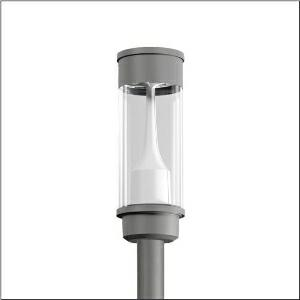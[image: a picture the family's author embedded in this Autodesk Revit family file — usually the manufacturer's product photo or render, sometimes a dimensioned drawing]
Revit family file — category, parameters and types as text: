
# Revit family: litepole_iq___pl1_2s_5xa5415of14h_b306
name_source: partatom
category: Lighting Fixtures
units: mm (PartAtom-declared; Revit-internal decimal feet)

## family parameters
Cut with Voids When Loaded = No
Host = Face
Light Source = No
Part Type = Normal
Room Calculation Point = No
Round Connector Dimension = Use Diameter
Shared = No

## types (1)
- --- (1 x LED, 2970 lm, 21.8 W, 2700K)
    Apparent Load = 22 VA
    CIE Flux Codes = 23 62 94 96 100
    Color Rendering = 70
    Color Temperature = 2700K
    Default Elevation = 1800 mm
    Description = Litepole iQ, mast luminaire, Module 540 iQ-SR, primary light control with 3 zone facetted reflector, of plastic, silver coated, highly specular, structured, primary optical cover: cover, of PMMA, transparent, partly coated, light distribution: PL1.2s, light emission: direct distribution, primary light characteristic: symmetric, installation type: post-top, LED, High Power LED, rated luminous flux: 2.970lm, luminous efficacy: 136lm/W, light colour: 727, colour temperature: 2700K, control gear: iQ Street-Remote, control: optimised constant luminous flux control (CLO 2.0), Desk-Remote (wireless, voltage-free reading and setting of iQ features in the workshop via application-optimized NFC function/RFID function), Light-Fading, Smart-Wire, Night-Set, Lumen-Switch, Temp-Guard, Auto-Match, Street-Remote, pre-setting: logarithmic dimming characteristic, with terminal, 6-pole, max. 2.5mm², mains connection: 230..240V, AC, 50/60Hz, start of lifetime: 22W, end of service life: 23W, reduction: 11W, luminaire housing, upper part, of glass-fibre reinforced polyester, coated, Siteco® metallic grey (DB 702S), diameter: 210mm, height: 590mm, spigot size: d x l = 76 x 70mm (post-top) | with reducer (optional accessory) 60 x 70mm, mounting height: 3..5m, post-top mast mounting element, of diecast aluminium, coated, Siteco® metallic grey (DB 702S), Module 540 iQ-SR, traffic white (RAL 9016), equipment: standard, protection rating (complete): IP65, insulation class (complete): insulation class II (safety insulation), certification: CE, ENEC, VDE, packaging unit: 1 piece

Light Distribution: PL1.2s
    Height = 590 mm
    Lamp = 1 x LED
    Lamp Light Flux = 2970 lm
    Lamp Power = 21.8 W
    Lamp count = 1
    Length = 220 mm
    Luminous efficacy = 136 lm/W
    Manufacturer = Siteco
    ModVariant = No
    Model = 5XA5415OF14H
    Number of Poles = 1
    OnlyDefault = Yes
    Power Factor = 1
    Product Name = Litepole iQ | PL1.2s
    Product group = mast luminaire | pylon top
    ProductGroupID = 6100
    Protection Class = Protection class II
    Protection Degree = IP 65
    RLX_Detail_Level = 1
    RLX_Emergency_Light_Flux = 0 lm
    RLX_Emergency_Type = 0
    RLX_Emergency_Type_DB = No
    RlxData = <blob elided: 40057 chars, md5=e18988a2>
    Socket = socket
    Standby Power = 0 W
    System Light Flux = 2970 lm
    System Power = 22 W
    Type Comments = factory setting: luminous flux: 100 % | dim-lin: 254 | 456 mA
    Type Image = l_1006025.jpg
    URL = http://relux.com
    VarID = @adj_144215
    Voltage = 0 V
    Weight = 0.00 kg
    Width = 0 mm  [stored 0 ft]

note: [stored X ft] marks values corroborated as IEEE doubles in the binary element streams (Revit-internal decimal feet)

## geometry (parser evidence)
native form markers: Blend x4, Sweep x8
no freeform markers — native parametric forms only
